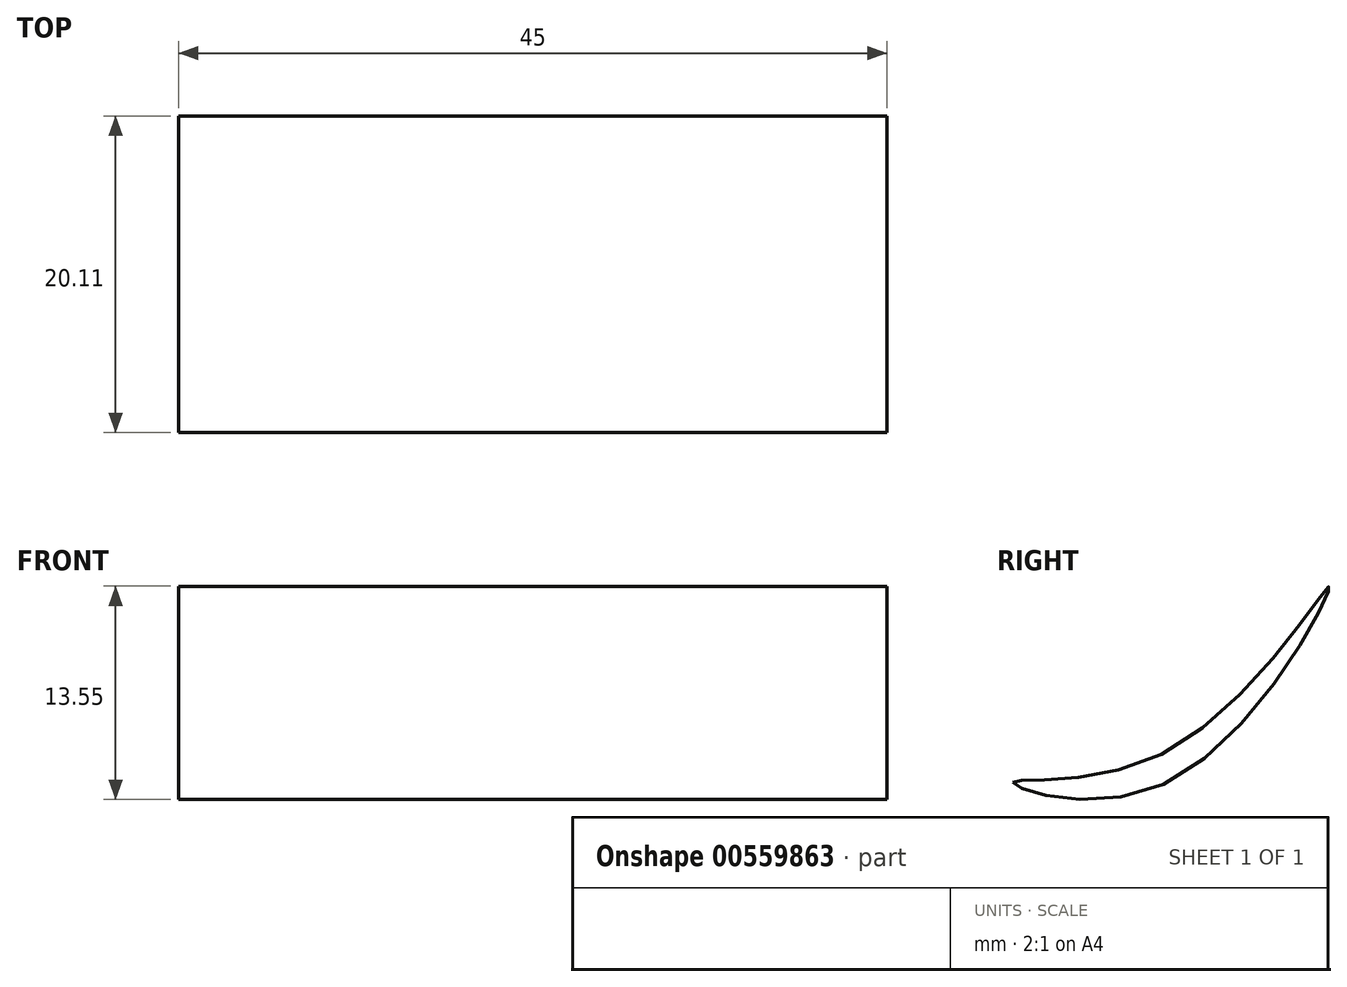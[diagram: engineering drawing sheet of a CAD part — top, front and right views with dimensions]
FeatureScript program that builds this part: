
annotation { "Feature Type Name" : "Feature", "Feature Type Description" : "" }
export const myFeature = defineFeature(function(context is Context, id is Id, definition is map)
    precondition{}
    {
        {
            var Q0;
            Q0=qCreatedBy(makeId("Right.planeOp"),FACE);
            var sketch = newSketch(context, id + "F0", { "sketchPlane" : qUnion([Q0])});
            skFitSpline(sketch, "E0", {"points": [v(-9.77, 10.62) * mm, v(0, 10.62) * mm, v(10.34, 23.09) * mm, v(0, 12.6) * mm, v(-9.77, 10.62) * mm]});
            skSolve(sketch);
        }
        {
            var Q0;
            Q0=makeQuery(id+"F0.imprint","IMPRINT",FACE,{"disambiguationData":[TD([[makeQuery(id+"F0.imprint","IMPRINT",EDGE,{"derivedFrom":sQuery(id+"F0.wireOp",EDGE,"E0")}),1.0]])]});
            extrude(context, id + "F1", {"entities" : qUnion([Q0]), "depth" : 45 * mm, "offsetDistance" : 25 * mm});
        }
    });
